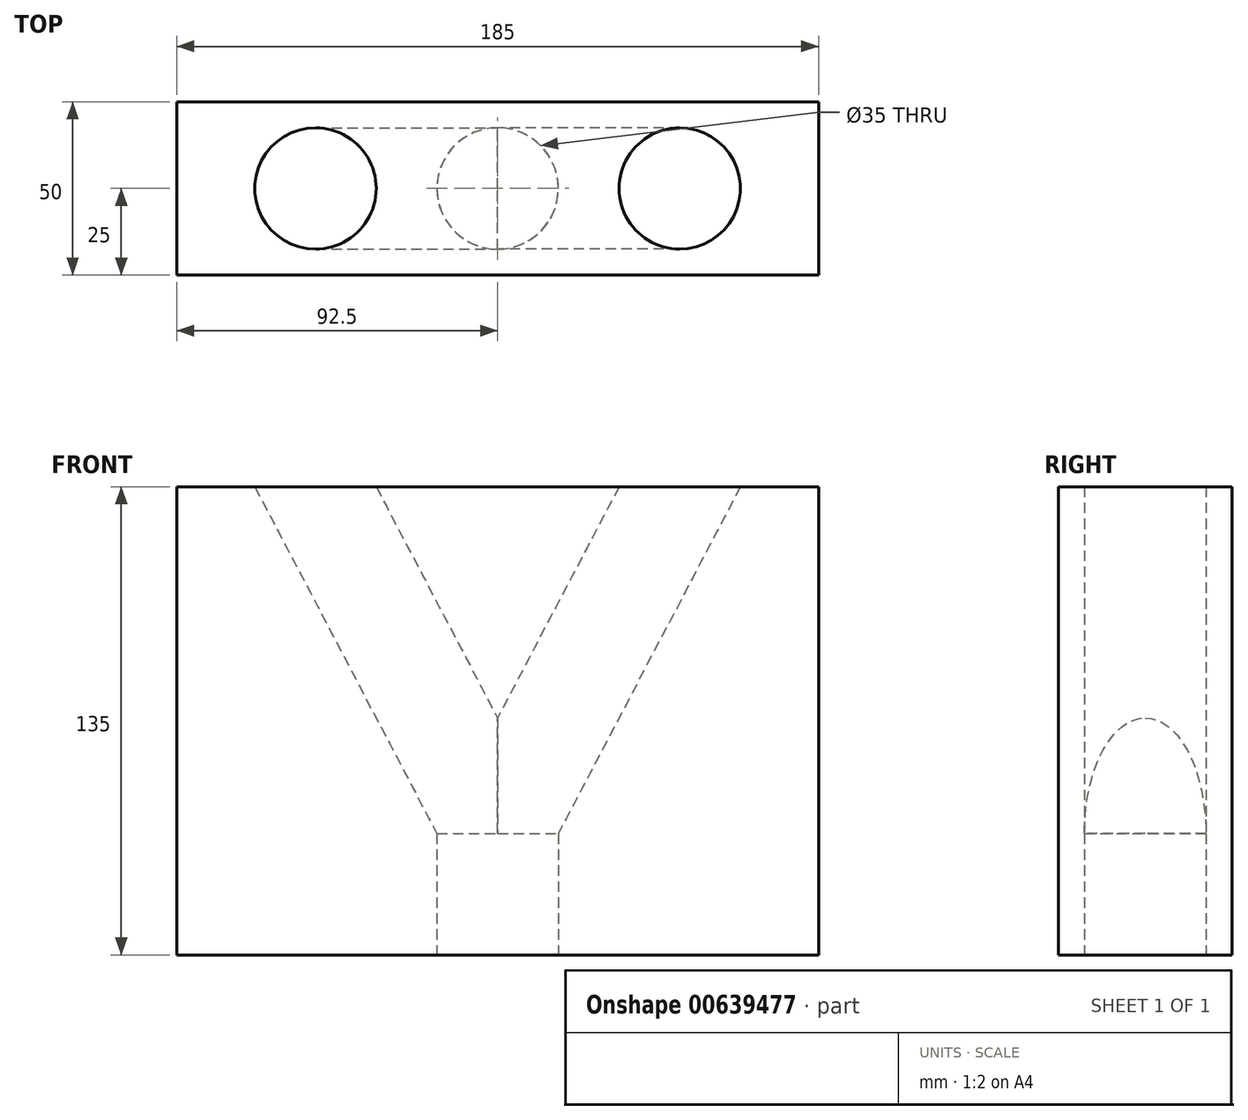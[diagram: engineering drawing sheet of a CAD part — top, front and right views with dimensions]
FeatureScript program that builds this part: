
annotation { "Feature Type Name" : "Feature", "Feature Type Description" : "" }
export const myFeature = defineFeature(function(context is Context, id is Id, definition is map)
    precondition{}
    {
        {
            var Q0;
            Q0=qCreatedBy(makeId("Top.planeOp"),FACE);
            var sketch = newSketch(context, id + "F0", { "sketchPlane" : qUnion([Q0])});
            skLineSegment(sketch, "E0.bottom", {"start": v(0, 0) * mm, "end": v(185, 0) * mm});
            skLineSegment(sketch, "E0.top", {"start": v(0, 50) * mm, "end": v(185, 50) * mm});
            skLineSegment(sketch, "E0.left", {"start": v(0, 0) * mm, "end": v(0, 50) * mm});
            skLineSegment(sketch, "E0.right", {"start": v(185, 0) * mm, "end": v(185, 50) * mm});
            skSolve(sketch);
        }
        {
            var Q0;
            Q0=qSketchRegion(id+"F0",true);
            extrude(context, id + "F1", {"entities" : qUnion([Q0]), "depth" : 135 * mm, "offsetDistance" : 25 * mm});
        }
        {
            var Q0;
            Q0=makeQuery(id+"F1.opExtrude","CAP_FACE",FACE,{"disambiguationData":[OSD([sQuery(id+"F0.wireOp",EDGE,"E0.bottom"),sQuery(id+"F0.wireOp",EDGE,"E0.top"),sQuery(id+"F0.wireOp",EDGE,"E0.left"),sQuery(id+"F0.wireOp",EDGE,"E0.right")])],"isStart":false});
            var sketch = newSketch(context, id + "F2", { "sketchPlane" : qUnion([Q0])});
            skEllipse(sketch, "E1", {"center": v(40, 25) * mm, "majorRadius": 17.5 * mm, "minorRadius": 17.5 * mm, "majorAxis": v(0, -1)});
            skLineSegment(sketch, "E2", {"start": v(92.5, 50) * mm, "end": v(92.5, 0) * mm, "construction": true});
            skEllipse(sketch, "E3.MirrorC", {"center": v(145, 25) * mm, "majorRadius": 17.5 * mm, "minorRadius": 17.5 * mm, "majorAxis": v(0, -1)});
            skSolve(sketch);
        }
        {
            var Q0;
            Q0=makeQuery(id+"F1.opExtrude","CAP_FACE",FACE,{"disambiguationData":[OSD([sQuery(id+"F0.wireOp",EDGE,"E0.bottom"),sQuery(id+"F0.wireOp",EDGE,"E0.top"),sQuery(id+"F0.wireOp",EDGE,"E0.left"),sQuery(id+"F0.wireOp",EDGE,"E0.right")])],"isStart":true});
            var sketch = newSketch(context, id + "F3", { "sketchPlane" : qUnion([Q0])});
            skPoint(sketch, "E4.0", {"position": v(92.5, -25) * mm});
            skCircle(sketch, "E5", {"center": v(92.5, -25) * mm, "radius": 17.5 * mm});
            skSolve(sketch);
        }
        {
            var Q0;
            Q0=qSketchRegion(id+"F3",true);
            extrude(context, id + "F4", {"entities" : qUnion([Q0]), "operationType" : NewBodyOperationType.REMOVE, "oppositeDirection" : true, "depth" : 35 * mm, "offsetDistance" : 25 * mm});
        }
        {
            var Q0;
            Q0=makeQuery(id+"F1.opExtrude","SWEPT_FACE",FACE,{"disambiguationData":[OSD([sQuery(id+"F0.wireOp",EDGE,"E0.bottom")])]});
            var sketch = newSketch(context, id + "F5", { "sketchPlane" : qUnion([Q0])});
            skLineSegment(sketch, "E6.0", {"start": v(22.5, 135) * mm, "end": v(57.5, 135) * mm});
            skLineSegment(sketch, "E7.0", {"start": v(127.5, 135) * mm, "end": v(162.5, 135) * mm});
            skLineSegment(sketch, "E8.0", {"start": v(110, 35) * mm, "end": v(75, 35) * mm});
            skLineSegment(sketch, "E9", {"start": v(162.23, 167.8) * mm, "end": v(92.5, 35) * mm});
            skLineSegment(sketch, "E10", {"start": v(92.5, 35) * mm, "end": v(22.77, 167.8) * mm});
            skSolve(sketch);
        }
        {
            var Q0;
            Q0=makeQuery(id+"F2.imprint","IMPRINT",FACE,{"disambiguationData":[TD([[makeQuery(id+"F2.imprint","IMPRINT",EDGE,{"derivedFrom":sQuery(id+"F2.wireOp",EDGE,"E1")}),1.0]])]});
            var Q1;
            Q1=makeQuery(id+"F2.imprint","IMPRINT",FACE,{"disambiguationData":[TD([[makeQuery(id+"F2.imprint","IMPRINT",EDGE,{"derivedFrom":sQuery(id+"F2.wireOp",EDGE,"E3.MirrorC")}),1.0]])]});
            var Q2;
            Q2=sQuery(id+"F2.wireOp",EDGE,"E1");
            var Q3;
            Q3=sQuery(id+"F2.wireOp",EDGE,"E3.MirrorC");
            var Q4;
            Q4=sQuery(id+"F5.wireOp",EDGE,"E10");
            var Q5;
            Q5=sQuery(id+"F5.wireOp",EDGE,"E9");
            sweep(context, id + "F6", {"operationType" : NewBodyOperationType.REMOVE, "profiles" : qUnion([Q0, Q1]), "surfaceProfiles" : qUnion([Q2, Q3]), "path" : qUnion([Q4, Q5])});
        }
    });
